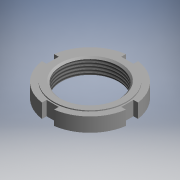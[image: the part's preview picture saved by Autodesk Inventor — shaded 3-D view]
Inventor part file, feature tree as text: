
AUTODESK INVENTOR PART (.ipt)
format: ipt  version: 2017.3 (Build 213256000, 256)  size: 148,992 bytes
history: native  units: mm (DEFAULTED — no unit token found)
features: other x14, sketch x4, revolve x3, thread x1, extrude x1
ambient origin geometry x8: Origin, YZ Plane, XZ Plane, XY Plane, X Axis, Y Axis, Z Axis, Center Point
bodies: Solid1 (feature_tree)
feature tree (23):
  revolve  "Revolution1"  Angle=360.0deg
  revolve  "Revolution2"  Angle=360.0deg
  thread  "Thread1"  [1 undecoded]
  revolve  "Revolution3"  [1 undecoded]
  extrude  "Extrusion1"  [1 undecoded]
  other  "FDT_CYLINDER_XY"
  other  "FDT_CYLINDER_YZ"
  other  "FDT_CYLINDER_ZX"
  other  "FDT_CYLINDER_X"
  other  "FDT_CYLINDER_Y"
  other  "FDT_CYLINDER_Z"
  other  "FDT_CYLINDER_Center"
  other  "NUT_XY"
  other  "NUT_YZ"
  other  "NUT_ZX"
  other  "NUT_X"
  other  "NUT_Y"
  other  "NUT_Z"
  other  "NUT_Center"
  sketch  "Sketch_1"  dims[d0=360.0deg d1=360.0deg]
  sketch  "Sketch_2"  dims[d2=6.71919mm d3=0.0mm d4=360.0deg d5=8.0mm d6=0.0mm]
  sketch  "Sketch_6"
  sketch  "Sketch_3"  dims[d7=0.0mm d8=0.0mm]
note: 3 required parameter values undecoded (feature->parameter linkage not recoverable at this tier; creation-order binding heuristic only, values carry confidence <= 0.55)
